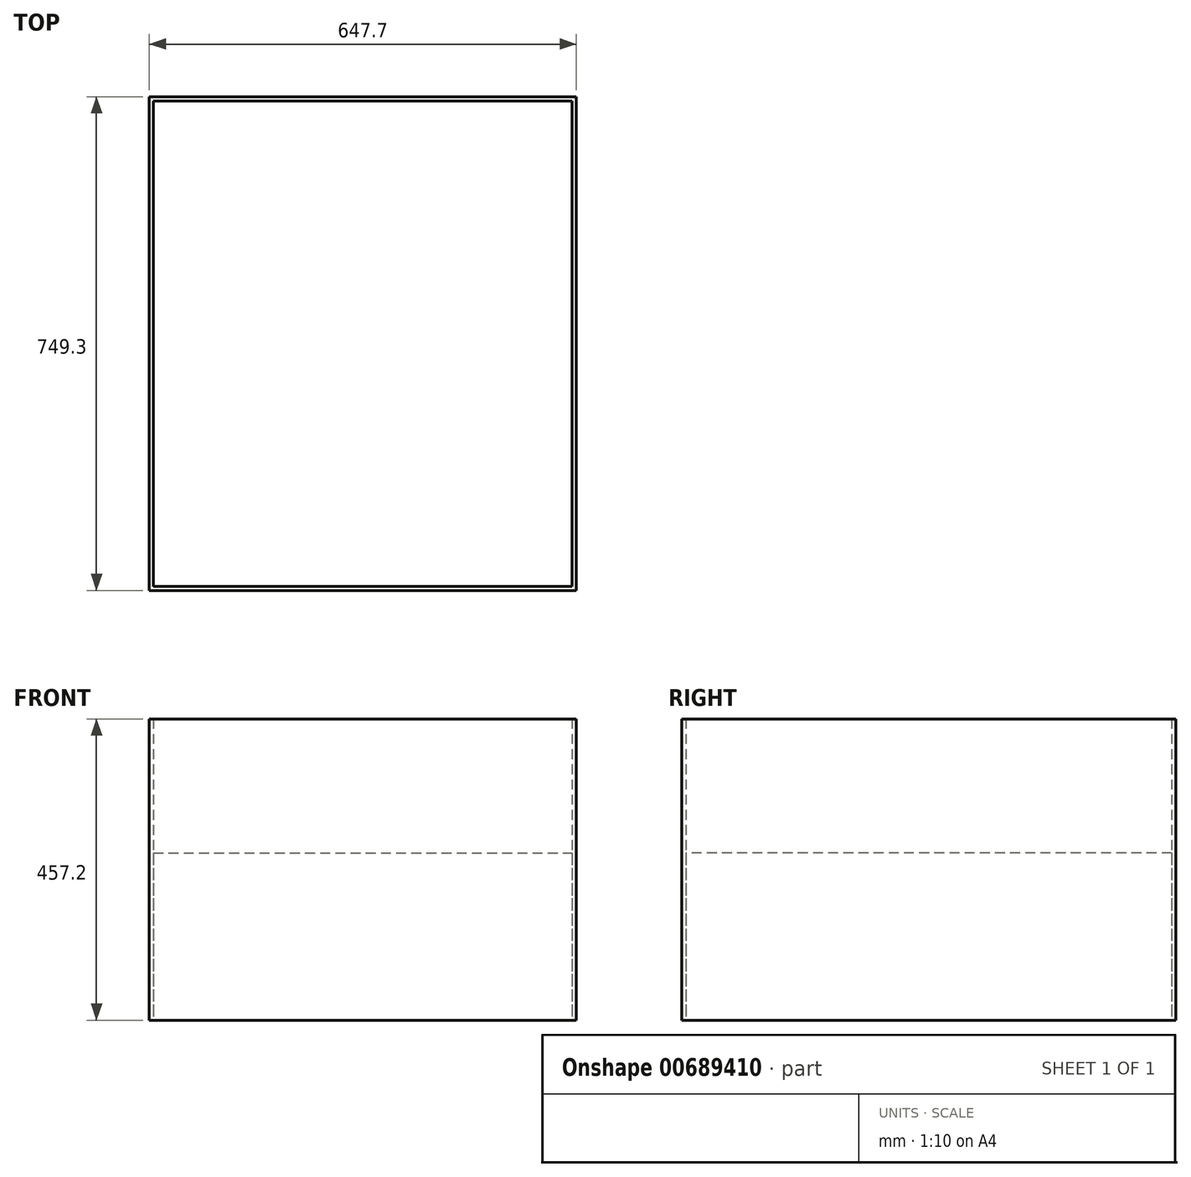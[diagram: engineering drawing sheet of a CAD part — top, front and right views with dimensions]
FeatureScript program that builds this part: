
annotation { "Feature Type Name" : "Feature", "Feature Type Description" : "" }
export const myFeature = defineFeature(function(context is Context, id is Id, definition is map)
    precondition{}
    {
        {
            var Q0;
            Q0=qCreatedBy(makeId("Top.planeOp"),FACE);
            var sketch = newSketch(context, id + "F0", { "sketchPlane" : qUnion([Q0])});
            skLineSegment(sketch, "E0.bottom", {"start": v(-323.85, 374.65) * mm, "end": v(323.85, 374.65) * mm});
            skLineSegment(sketch, "E0.top", {"start": v(-323.85, -374.65) * mm, "end": v(323.85, -374.65) * mm});
            skLineSegment(sketch, "E0.left", {"start": v(-323.85, 374.65) * mm, "end": v(-323.85, -374.65) * mm});
            skLineSegment(sketch, "E0.right", {"start": v(323.85, 374.65) * mm, "end": v(323.85, -374.65) * mm});
            skPoint(sketch, "E0.middle", {"position": v(0, 0) * mm});
            skLineSegment(sketch, "E1.bottom", {"start": v(-317.5, 368.3) * mm, "end": v(317.5, 368.3) * mm});
            skLineSegment(sketch, "E1.top", {"start": v(-317.5, -368.3) * mm, "end": v(317.5, -368.3) * mm});
            skLineSegment(sketch, "E1.left", {"start": v(-317.5, 368.3) * mm, "end": v(-317.5, -368.3) * mm});
            skLineSegment(sketch, "E1.right", {"start": v(317.5, 368.3) * mm, "end": v(317.5, -368.3) * mm});
            skSolve(sketch);
        }
        {
            var Q0;
            Q0=makeQuery(id+"F0.imprint","IMPRINT",FACE,{"disambiguationData":[TD([[makeQuery(id+"F0.imprint","IMPRINT",EDGE,{"derivedFrom":sQuery(id+"F0.wireOp",EDGE,"E0.bottom")}),-1.0]])]});
            extrude(context, id + "F1", {"entities" : qUnion([Q0]), "depth" : 457.2 * mm, "offsetDistance" : 25.4 * mm});
        }
        {
            var Q0;
            Q0=qCreatedBy(makeId("Top.planeOp"),FACE);
            var sketch = newSketch(context, id + "F2", { "sketchPlane" : qUnion([Q0])});
            skLineSegment(sketch, "E2.bottom", {"start": v(-317.5, 368.3) * mm, "end": v(317.5, 368.3) * mm});
            skLineSegment(sketch, "E2.top", {"start": v(-317.5, -368.3) * mm, "end": v(317.5, -368.3) * mm});
            skLineSegment(sketch, "E2.left", {"start": v(-317.5, 368.3) * mm, "end": v(-317.5, -368.3) * mm});
            skLineSegment(sketch, "E2.right", {"start": v(317.5, 368.3) * mm, "end": v(317.5, -368.3) * mm});
            skPoint(sketch, "E2.middle", {"position": v(0, 0) * mm});
            skSolve(sketch);
        }
        {
            var Q0;
            Q0=makeQuery(id+"F2.imprint","IMPRINT",FACE,{"disambiguationData":[TD([[makeQuery(id+"F2.imprint","IMPRINT",EDGE,{"derivedFrom":sQuery(id+"F2.wireOp",EDGE,"E2.bottom")}),-1.0]])]});
            extrude(context, id + "F3", {"entities" : qUnion([Q0]), "depth" : 254 * mm, "offsetDistance" : 25.4 * mm});
        }
    });
